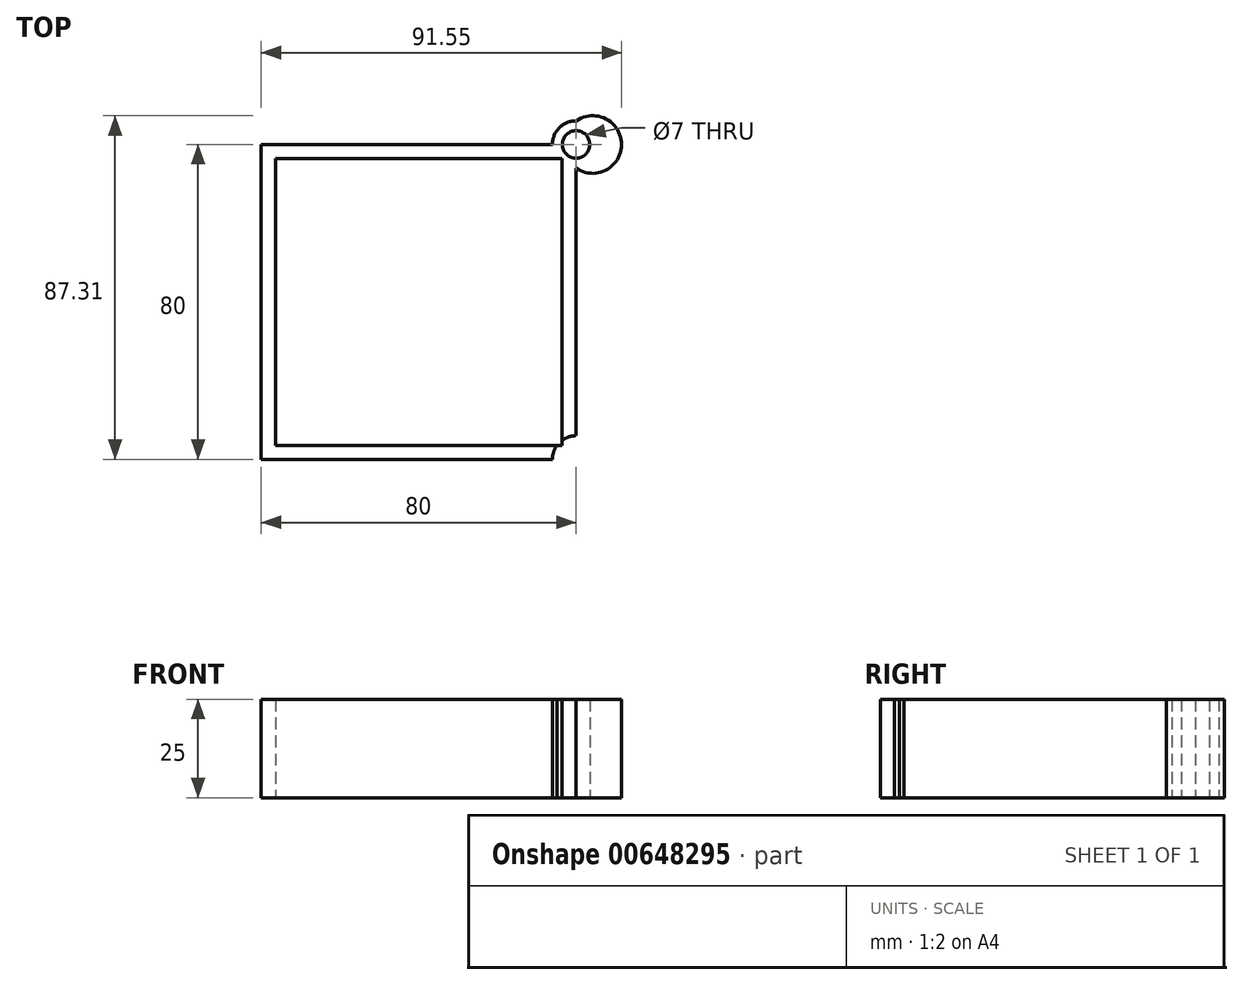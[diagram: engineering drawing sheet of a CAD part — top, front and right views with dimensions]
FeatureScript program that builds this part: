
annotation { "Feature Type Name" : "Feature", "Feature Type Description" : "" }
export const myFeature = defineFeature(function(context is Context, id is Id, definition is map)
    precondition{}
    {
        {
            var Q0;
            Q0=qCreatedBy(makeId("Top.planeOp"),FACE);
            var sketch = newSketch(context, id + "F0", { "sketchPlane" : qUnion([Q0])});
            skLineSegment(sketch, "E0.bottom", {"start": v(-36.38, 36.45) * mm, "end": v(36.38, 36.45) * mm});
            skLineSegment(sketch, "E0.top", {"start": v(-36.38, -36.45) * mm, "end": v(36.38, -36.45) * mm});
            skLineSegment(sketch, "E0.left", {"start": v(-36.38, 36.45) * mm, "end": v(-36.38, -36.45) * mm});
            skLineSegment(sketch, "E0.right", {"start": v(36.38, 36.45) * mm, "end": v(36.38, -36.45) * mm});
            skPoint(sketch, "E0.middle", {"position": v(0, 0) * mm});
            skSolve(sketch);
        }
        {
            var Q0;
            Q0=makeQuery(id+"F0.imprint","IMPRINT",FACE,{"disambiguationData":[TD([[makeQuery(id+"F0.imprint","IMPRINT",EDGE,{"derivedFrom":sQuery(id+"F0.wireOp",EDGE,"E0.bottom")}),-1.0]])]});
            var sketch = newSketch(context, id + "F1", { "sketchPlane" : qUnion([Q0])});
            skLineSegment(sketch, "E1.bottom", {"start": v(40, -40) * mm, "end": v(-40, -40) * mm});
            skLineSegment(sketch, "E1.top", {"start": v(34, 40) * mm, "end": v(-40, 40) * mm});
            skLineSegment(sketch, "E1.left", {"start": v(40, -40) * mm, "end": v(40, 34) * mm});
            skLineSegment(sketch, "E1.right", {"start": v(-40, -40) * mm, "end": v(-40, 40) * mm});
            skPoint(sketch, "E1.middle", {"position": v(0, 0) * mm});
            skCircle(sketch, "E2", {"center": v(40, 40) * mm, "radius": 3.5 * mm});
            skArc(sketch, "E3", {"start": v(40.04, 46) * mm, "mid": v(35.77, 44.26) * mm, "end": v(34, 40) * mm});
            skCircle(sketch, "E4.MirrorC", {"center": v(40, -40) * mm, "radius": 6 * mm});
            skArc(sketch, "E5", {"start": v(40, 34) * mm, "mid": v(51.55, 39.96) * mm, "end": v(40.04, 46) * mm});
            skLineSegment(sketch, "E6.bottom", {"start": v(-24.48, 29) * mm, "end": v(-8.2, 29) * mm});
            skLineSegment(sketch, "E6.top", {"start": v(-24.48, -26.83) * mm, "end": v(-8.2, -26.83) * mm});
            skLineSegment(sketch, "E6.left", {"start": v(-24.48, 29) * mm, "end": v(-24.48, -26.83) * mm});
            skLineSegment(sketch, "E6.right", {"start": v(-8.2, 29) * mm, "end": v(-8.2, -26.83) * mm});
            skLineSegment(sketch, "E7.bottom", {"start": v(8.55, 27.38) * mm, "end": v(21.58, 27.38) * mm});
            skLineSegment(sketch, "E7.top", {"start": v(8.55, -16.36) * mm, "end": v(21.58, -16.36) * mm});
            skLineSegment(sketch, "E7.left", {"start": v(8.55, 27.38) * mm, "end": v(8.55, -16.36) * mm});
            skLineSegment(sketch, "E7.right", {"start": v(21.58, 27.38) * mm, "end": v(21.58, -16.36) * mm});
            skLineSegment(sketch, "E8.bottom", {"start": v(-32.65, 65.71) * mm, "end": v(-7.31, 65.71) * mm});
            skLineSegment(sketch, "E8.top", {"start": v(-32.65, 45.97) * mm, "end": v(-7.31, 45.97) * mm});
            skLineSegment(sketch, "E8.left", {"start": v(-32.65, 65.71) * mm, "end": v(-32.65, 45.97) * mm});
            skLineSegment(sketch, "E8.right", {"start": v(-7.31, 65.71) * mm, "end": v(-7.31, 45.97) * mm});
            skSolve(sketch);
        }
        {
            var Q0;
            Q0=makeQuery(id+"F0.imprint","IMPRINT",FACE,{"disambiguationData":[TD([[makeQuery(id+"F0.imprint","IMPRINT",EDGE,{"derivedFrom":sQuery(id+"F0.wireOp",EDGE,"E0.bottom")}),-1.0]])]});
            var Q1;
            Q1=makeQuery(id+"F1.imprint","IMPRINT",FACE,{"disambiguationData":[TD([[makeQuery(id+"F1.imprint","IMPRINT",EDGE,{"derivedFrom":sQuery(id+"F1.wireOp",EDGE,"E1.top")}),1.0]])]});
            extrude(context, id + "F2", {"entities" : qUnion([Q0, Q1]), "depth" : 25 * mm, "offsetDistance" : 25 * mm});
        }
    });
